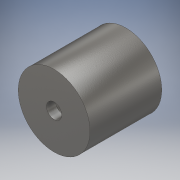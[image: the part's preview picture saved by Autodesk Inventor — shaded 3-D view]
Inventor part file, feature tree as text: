
AUTODESK INVENTOR PART (.ipt)
format: ipt  version: 2018.3 (Build 223284000, 284)  size: 124,928 bytes
history: native  units: mm
features: sketch x2, revolve x1, hole x1
ambient origin geometry x8: Origin, YZ Plane, XZ Plane, XY Plane, X Axis, Y Axis, Z Axis, Center Point
bodies: Volumenkörper1 (feature_tree)
feature tree (4):
  revolve  "Umdrehung1"
  hole  "Bohrung1"  [1 undecoded]
  sketch  "Skizze1"  dims[d0=6.0mm d1=20.0mm]
  sketch  "Skizze2"  dims[d2=10.0mm d3=90.0deg d4=8.5mm d5=6.0mm d6=4.0mm d7=2.0mm d8=90.0deg d9=8.0mm d10=20.594885mm d11=5.0mm d12=40.0mm]
note: 1 required parameter value undecoded (feature->parameter linkage not recoverable at this tier; creation-order binding heuristic only, values carry confidence <= 0.55)
